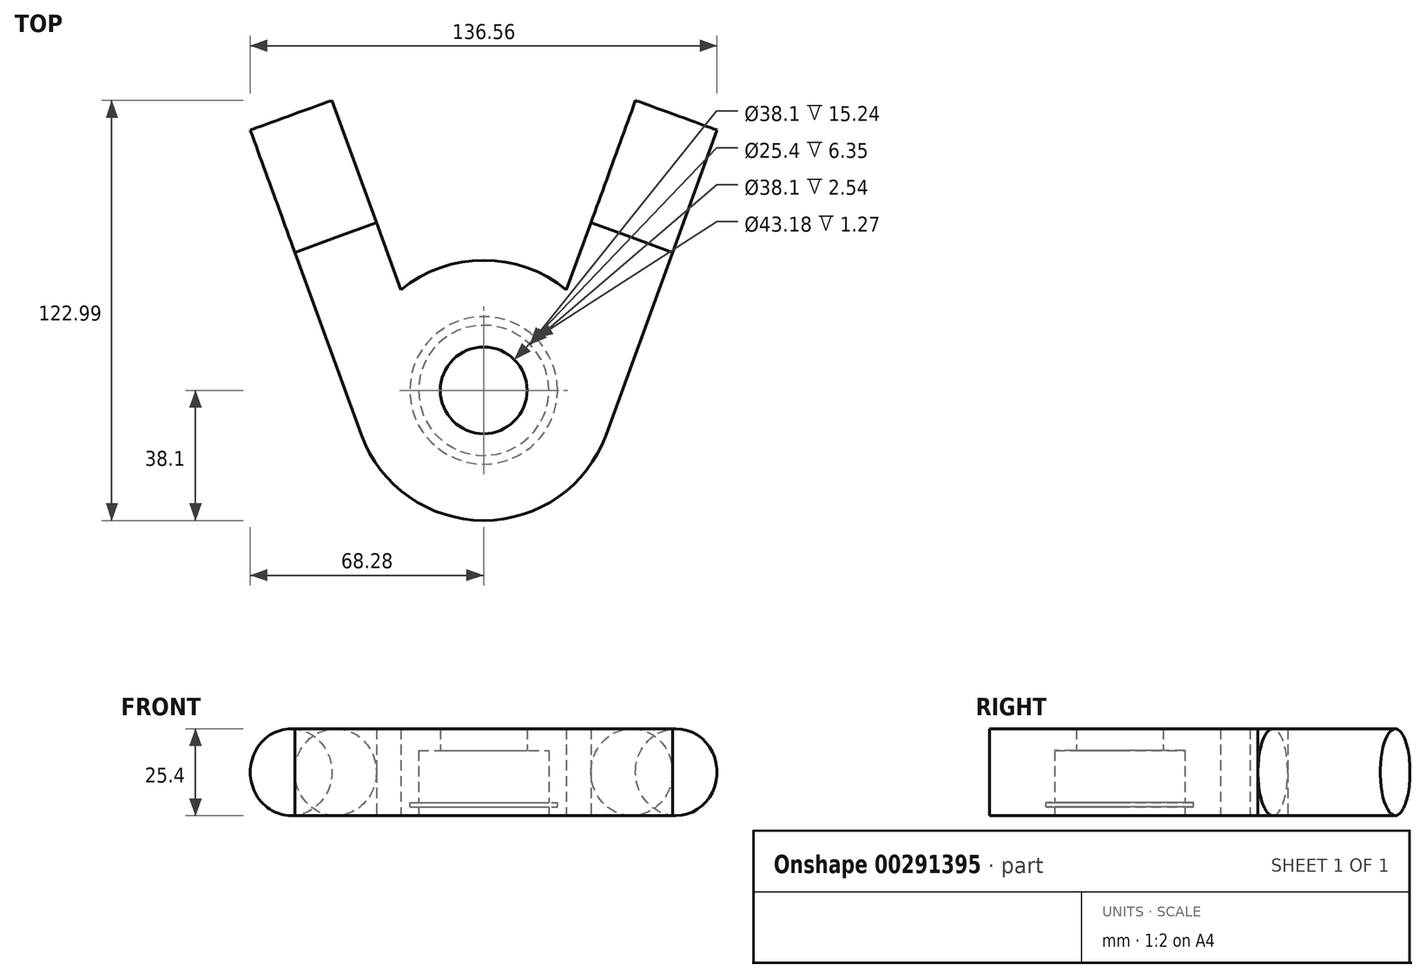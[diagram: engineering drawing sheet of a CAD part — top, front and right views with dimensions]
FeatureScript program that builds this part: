
annotation { "Feature Type Name" : "Feature", "Feature Type Description" : "" }
export const myFeature = defineFeature(function(context is Context, id is Id, definition is map)
    precondition{}
    {
        {
            var Q0;
            Q0=qCreatedBy(makeId("Top.planeOp"),FACE);
            var sketch = newSketch(context, id + "F0", { "sketchPlane" : qUnion([Q0])});
            skCircle(sketch, "E0", {"center": v(0, 0) * mm, "radius": 12.7 * mm});
            skCircle(sketch, "E1", {"center": v(0, 0) * mm, "radius": 38.1 * mm});
            skLineSegment(sketch, "E2", {"start": v(0, 0) * mm, "end": v(0, 76.2) * mm, "construction": true});
            skLineSegment(sketch, "E3", {"start": v(35.8, -13.03) * mm, "end": v(68.28, 76.2) * mm});
            skLineSegment(sketch, "E4", {"start": v(-35.8, -13.03) * mm, "end": v(-68.28, 76.2) * mm});
            skLineSegment(sketch, "E5", {"start": v(-24.22, 29.41) * mm, "end": v(-44.41, 84.89) * mm});
            skLineSegment(sketch, "E6", {"start": v(24.22, 29.41) * mm, "end": v(44.41, 84.89) * mm});
            skLineSegment(sketch, "E7", {"start": v(-68.28, 76.2) * mm, "end": v(-44.41, 84.89) * mm});
            skLineSegment(sketch, "E8", {"start": v(68.28, 76.2) * mm, "end": v(44.41, 84.89) * mm});
            skSolve(sketch);
        }
        {
            var Q0;
            Q0=makeQuery(id+"F0.imprint","IMPRINT",FACE,{"disambiguationData":[TD([[makeQuery(id+"F0.imprint","IMPRINT",EDGE,{"derivedFrom":sQuery(id+"F0.wireOp",EDGE,"E0")}),-1.0]])]});
            var Q1;
            {var subQ0=sQuery(id+"F0.wireOp",EDGE,"E4");Q1=makeQuery(id+"F0.imprint","IMPRINT",FACE,{"disambiguationData":[TD([[makeQuery(id+"F0.imprint","IMPRINT",EDGE,{"derivedFrom":subQ0}),-1.0]])]});}
            var Q2;
            {var subQ0=sQuery(id+"F0.wireOp",EDGE,"E3");Q2=makeQuery(id+"F0.imprint","IMPRINT",FACE,{"disambiguationData":[TD([[makeQuery(id+"F0.imprint","IMPRINT",EDGE,{"derivedFrom":subQ0}),1.0]])]});}
            extrude(context, id + "F1", {"entities" : qUnion([Q0, Q1, Q2]), "depth" : 25.4 * mm});
        }
        {
            var Q0;
            Q0=makeQuery(id+"F1.opExtrude","CAP_FACE",FACE,{"disambiguationData":[OSD([sQuery(id+"F0.wireOp",EDGE,"E0"),sQuery(id+"F0.wireOp",EDGE,"E1"),sQuery(id+"F0.wireOp",EDGE,"E3"),sQuery(id+"F0.wireOp",EDGE,"E4"),sQuery(id+"F0.wireOp",EDGE,"E5"),sQuery(id+"F0.wireOp",EDGE,"E6"),sQuery(id+"F0.wireOp",EDGE,"E7"),sQuery(id+"F0.wireOp",EDGE,"E8")])],"isStart":true});
            var sketch = newSketch(context, id + "F2", { "sketchPlane" : qUnion([Q0])});
            skCircle(sketch, "E9", {"center": v(0, 0) * mm, "radius": 19.05 * mm});
            skSolve(sketch);
        }
        {
            var Q0;
            Q0 = qSketchRegion(id + "F2", true);
            extrude(context, id + "F3", {"entities" : qUnion([Q0]), "operationType" : NewBodyOperationType.REMOVE, "oppositeDirection" : true, "depth" : 19.05 * mm});
        }
        {
            var Q0;
            Q0=makeQuery(id+"F3.boolean.opBoolean","COPY",FACE,{"derivedFrom":makeQuery(id+"F3.opExtrude","CAP_FACE",FACE,{"disambiguationData":[OSD([sQuery(id+"F2.wireOp",EDGE,"E9")])],"isStart":false})});
            cPlane(context, id + "F4", {"entities" : qUnion([Q0]), "cplaneType" : CPlaneType.OFFSET, "offset" : 15.24 * mm, "width" : 152.4 * mm, "height" : 152.4 * mm});
        }
        {
            var Q0;
            Q0=qCreatedBy(id+"F4.planeOp",FACE);
            var sketch = newSketch(context, id + "F5", { "sketchPlane" : qUnion([Q0])});
            skCircle(sketch, "E10", {"center": v(0, 0) * mm, "radius": 21.59 * mm});
            skSolve(sketch);
        }
        {
            var Q0;
            Q0=makeQuery(id+"F1.opExtrude","SWEPT_FACE",FACE,{"disambiguationData":[OSD([sQuery(id+"F0.wireOp",EDGE,"E8")])]});
            var sketch = newSketch(context, id + "F6", { "sketchPlane" : qUnion([Q0])});
            skCircle(sketch, "E11", {"center": v(-25.4, 12.7) * mm, "radius": 12.7 * mm});
            skPoint(sketch, "E11.centerSnap0", {"position": v(-38.1, 12.7) * mm});
            skPoint(sketch, "E11.centerSnap1", {"position": v(-25.4, 0) * mm});
            skSolve(sketch);
        }
        {
            var Q0;
            {var subQ0=sQuery(id+"F6.wireOp",EDGE,"E11");var subQ1=sQuery(id+"F0.wireOp",EDGE,"E8");var subQ2=makeQuery(id+"F1.opExtrude","CAP_EDGE",EDGE,{"disambiguationData":[OSD([subQ1])],"isStart":false});var subQ3=makeQuery(id+"F6.imprint","INTERSECT",VERTEX,{"derivedFrom":[subQ2,subQ0]});Q0=makeQuery(id+"F6.imprint","IMPRINT",FACE,{"disambiguationData":[TD([[makeQuery(id+"F6.imprint","IMPRINT",EDGE,{"disambiguationData":[TD([[subQ3,-1.0]])],"derivedFrom":subQ0}),-1.0]])]});}
            var Q1;
            {var subQ0=sQuery(id+"F6.wireOp",EDGE,"E11");var subQ1=sQuery(id+"F0.wireOp",EDGE,"E8");var subQ2=makeQuery(id+"F1.opExtrude","CAP_EDGE",EDGE,{"disambiguationData":[OSD([subQ1])],"isStart":false});var subQ3=makeQuery(id+"F6.imprint","INTERSECT",VERTEX,{"derivedFrom":[subQ2,subQ0]});Q1=makeQuery(id+"F6.imprint","IMPRINT",FACE,{"disambiguationData":[TD([[makeQuery(id+"F6.imprint","IMPRINT",EDGE,{"disambiguationData":[TD([[subQ3,1.0]])],"derivedFrom":subQ0}),-1.0]])]});}
            var Q2;
            {var subQ0=sQuery(id+"F6.wireOp",EDGE,"E11");var subQ1=sQuery(id+"F0.wireOp",EDGE,"E8");var subQ4=makeQuery(id+"F1.opExtrude","CAP_EDGE",EDGE,{"disambiguationData":[OSD([subQ1])],"isStart":true});var subQ5=makeQuery(id+"F6.imprint","INTERSECT",VERTEX,{"derivedFrom":[subQ4,subQ0]});Q2=makeQuery(id+"F6.imprint","IMPRINT",FACE,{"disambiguationData":[TD([[makeQuery(id+"F6.imprint","IMPRINT",EDGE,{"disambiguationData":[TD([[subQ5,-1.0]])],"derivedFrom":subQ0}),-1.0]])]});}
            var Q3;
            {var subQ0=sQuery(id+"F6.wireOp",EDGE,"E11");var subQ1=sQuery(id+"F0.wireOp",EDGE,"E8");var subQ4=makeQuery(id+"F1.opExtrude","CAP_EDGE",EDGE,{"disambiguationData":[OSD([subQ1])],"isStart":true});var subQ5=makeQuery(id+"F6.imprint","INTERSECT",VERTEX,{"derivedFrom":[subQ4,subQ0]});Q3=makeQuery(id+"F6.imprint","IMPRINT",FACE,{"disambiguationData":[TD([[makeQuery(id+"F6.imprint","IMPRINT",EDGE,{"disambiguationData":[TD([[subQ5,1.0]])],"derivedFrom":subQ0}),-1.0]])]});}
            extrude(context, id + "F7", {"entities" : qUnion([Q0, Q1, Q2, Q3]), "operationType" : NewBodyOperationType.REMOVE, "oppositeDirection" : true, "depth" : 38.1 * mm});
        }
        {
            var Q0;
            Q0 = qSketchRegion(id + "F5", true);
            extrude(context, id + "F8", {"entities" : qUnion([Q0]), "operationType" : NewBodyOperationType.REMOVE, "depth" : 1.27 * mm});
        }
        {
            var Q0;
            Q0=makeQuery(id+"F1.opExtrude","SWEPT_FACE",FACE,{"disambiguationData":[OSD([sQuery(id+"F0.wireOp",EDGE,"E7")])]});
            var sketch = newSketch(context, id + "F9", { "sketchPlane" : qUnion([Q0])});
            skCircle(sketch, "E12", {"center": v(25.4, 12.7) * mm, "radius": 12.7 * mm});
            skPoint(sketch, "E12.centerSnap0", {"position": v(12.7, 12.7) * mm});
            skPoint(sketch, "E12.centerSnap1", {"position": v(25.4, 25.4) * mm});
            skSolve(sketch);
        }
        {
            var Q0;
            {var subQ0=sQuery(id+"F9.wireOp",EDGE,"E12");var subQ1=sQuery(id+"F0.wireOp",EDGE,"E7");var subQ2=makeQuery(id+"F1.opExtrude","CAP_EDGE",EDGE,{"disambiguationData":[OSD([subQ1])],"isStart":false});var subQ3=makeQuery(id+"F9.imprint","INTERSECT",VERTEX,{"derivedFrom":[subQ2,subQ0]});Q0=makeQuery(id+"F9.imprint","IMPRINT",FACE,{"disambiguationData":[TD([[makeQuery(id+"F9.imprint","IMPRINT",EDGE,{"disambiguationData":[TD([[subQ3,-1.0]])],"derivedFrom":subQ0}),-1.0]])]});}
            var Q1;
            {var subQ0=sQuery(id+"F9.wireOp",EDGE,"E12");var subQ1=sQuery(id+"F0.wireOp",EDGE,"E7");var subQ2=makeQuery(id+"F1.opExtrude","CAP_EDGE",EDGE,{"disambiguationData":[OSD([subQ1])],"isStart":false});var subQ3=makeQuery(id+"F9.imprint","INTERSECT",VERTEX,{"derivedFrom":[subQ2,subQ0]});Q1=makeQuery(id+"F9.imprint","IMPRINT",FACE,{"disambiguationData":[TD([[makeQuery(id+"F9.imprint","IMPRINT",EDGE,{"disambiguationData":[TD([[subQ3,1.0]])],"derivedFrom":subQ0}),-1.0]])]});}
            var Q2;
            {var subQ0=sQuery(id+"F9.wireOp",EDGE,"E12");var subQ1=sQuery(id+"F0.wireOp",EDGE,"E7");var subQ4=makeQuery(id+"F1.opExtrude","CAP_EDGE",EDGE,{"disambiguationData":[OSD([subQ1])],"isStart":true});var subQ5=makeQuery(id+"F9.imprint","INTERSECT",VERTEX,{"derivedFrom":[subQ4,subQ0]});Q2=makeQuery(id+"F9.imprint","IMPRINT",FACE,{"disambiguationData":[TD([[makeQuery(id+"F9.imprint","IMPRINT",EDGE,{"disambiguationData":[TD([[subQ5,1.0]])],"derivedFrom":subQ0}),-1.0]])]});}
            var Q3;
            {var subQ0=sQuery(id+"F9.wireOp",EDGE,"E12");var subQ1=sQuery(id+"F0.wireOp",EDGE,"E7");var subQ4=makeQuery(id+"F1.opExtrude","CAP_EDGE",EDGE,{"disambiguationData":[OSD([subQ1])],"isStart":true});var subQ5=makeQuery(id+"F9.imprint","INTERSECT",VERTEX,{"derivedFrom":[subQ4,subQ0]});Q3=makeQuery(id+"F9.imprint","IMPRINT",FACE,{"disambiguationData":[TD([[makeQuery(id+"F9.imprint","IMPRINT",EDGE,{"disambiguationData":[TD([[subQ5,-1.0]])],"derivedFrom":subQ0}),-1.0]])]});}
            extrude(context, id + "F10", {"entities" : qUnion([Q0, Q1, Q2, Q3]), "operationType" : NewBodyOperationType.REMOVE, "oppositeDirection" : true, "depth" : 38.1 * mm});
        }
    });
